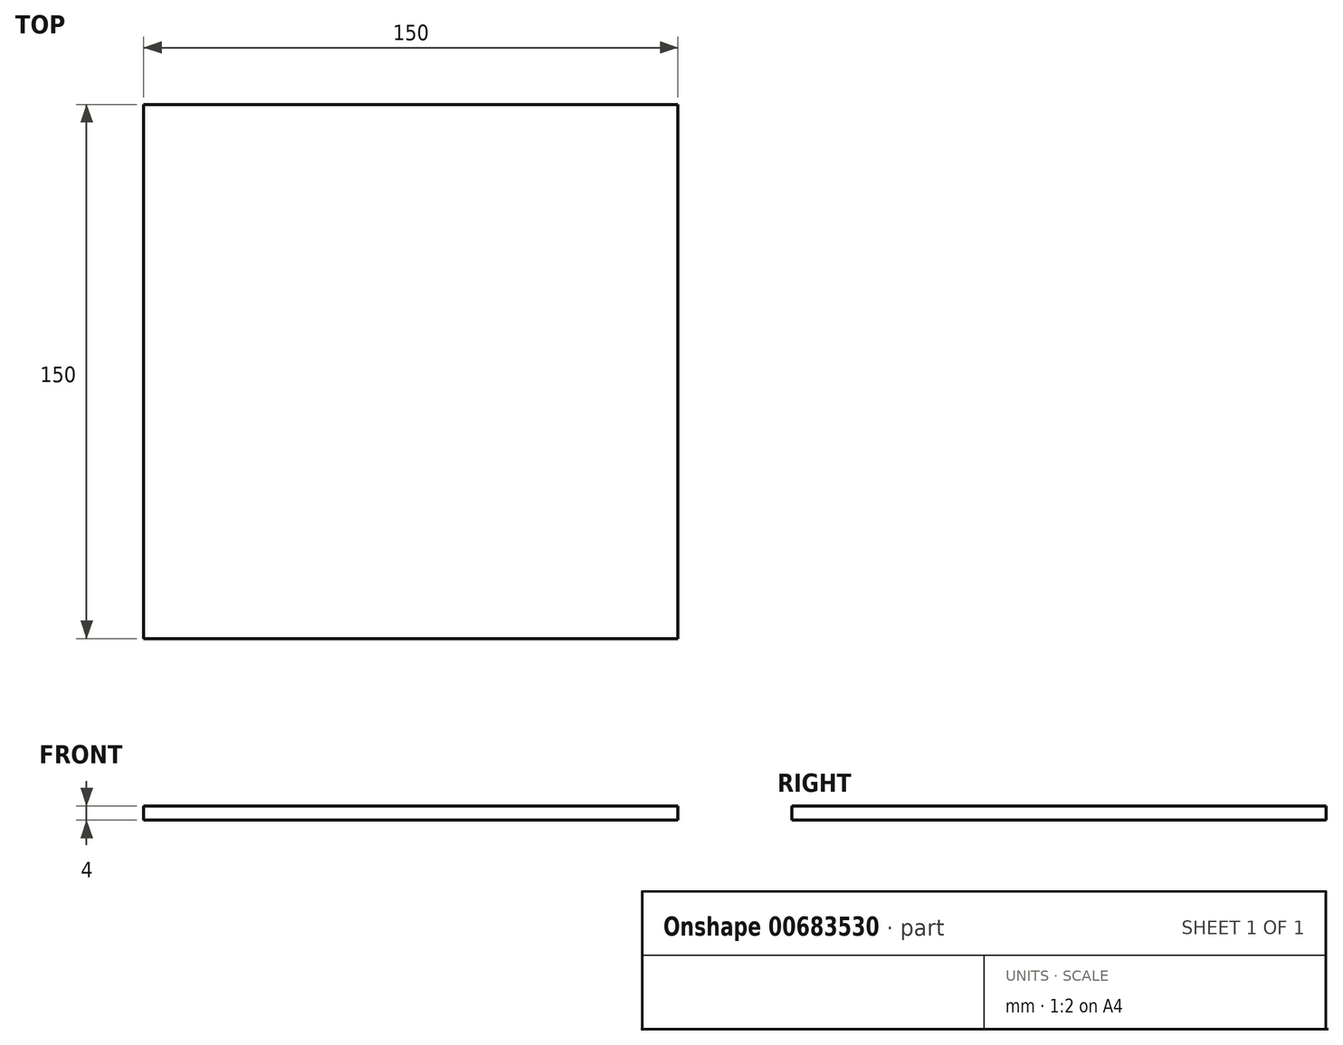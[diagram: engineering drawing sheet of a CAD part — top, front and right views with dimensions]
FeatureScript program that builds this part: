
annotation { "Feature Type Name" : "Feature", "Feature Type Description" : "" }
export const myFeature = defineFeature(function(context is Context, id is Id, definition is map)
    precondition{}
    {
        {
            var Q0;
            Q0=qCreatedBy(makeId("Top.planeOp"),FACE);
            var sketch = newSketch(context, id + "F0", { "sketchPlane" : qUnion([Q0])});
            skLineSegment(sketch, "E0.bottom", {"start": v(75, 75) * mm, "end": v(-75, 75) * mm});
            skLineSegment(sketch, "E0.top", {"start": v(75, -75) * mm, "end": v(-75, -75) * mm});
            skLineSegment(sketch, "E0.left", {"start": v(75, 75) * mm, "end": v(75, -75) * mm});
            skLineSegment(sketch, "E0.right", {"start": v(-75, 75) * mm, "end": v(-75, -75) * mm});
            skPoint(sketch, "E0.middle", {"position": v(0, 0) * mm});
            skSolve(sketch);
        }
        {
            var Q0;
            Q0 = qSketchRegion(id + "F0", true);
            extrude(context, id + "F1", {"entities" : qUnion([Q0]), "depth" : 4 * mm, "offsetDistance" : 25 * mm});
        }
    });
